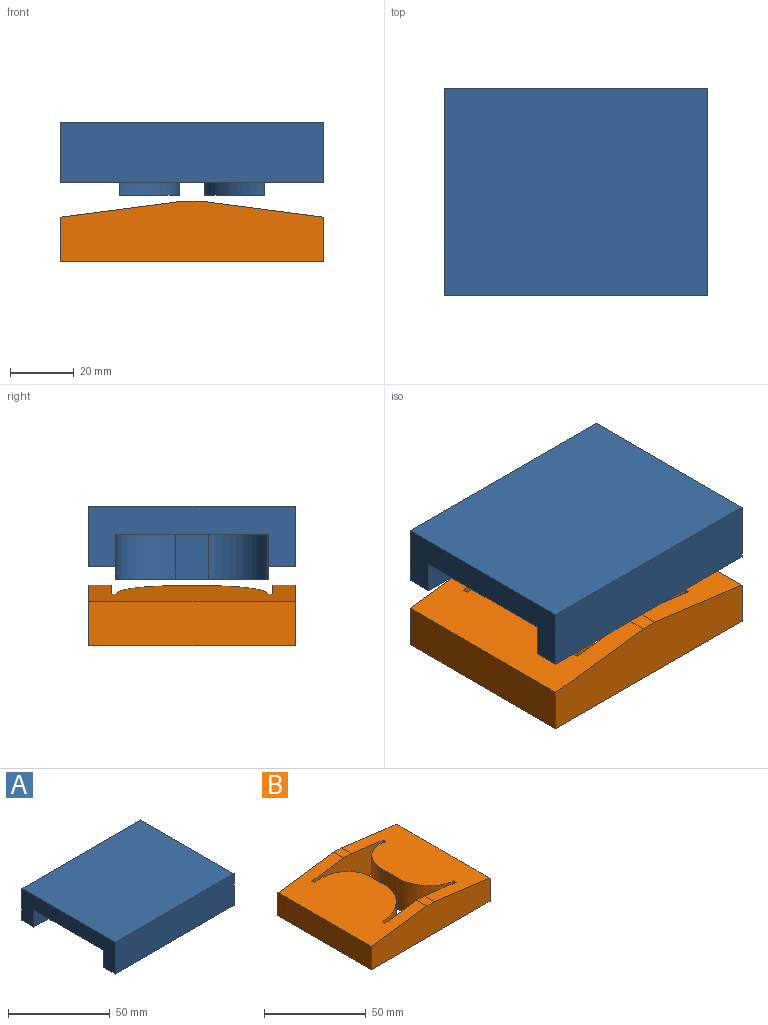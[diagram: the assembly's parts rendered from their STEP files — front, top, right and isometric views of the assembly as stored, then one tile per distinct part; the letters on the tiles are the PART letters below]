
ASSEMBLY  parts=2 mates=1
PART A: 30 faces, bbox 82.6x64.8x22.9 mm
  f0: plane 18.42x10.16mm, normal (0,-1,0), area 187.1mm2, adj f2,f8,f16,f28
  f1: plane 18.42x10.16mm, normal (0,1,0), area 187.1mm2, adj f2,f8,f15,f28
  f2: plane 64.77x19.05mm, normal (-1,0,0), area 743.5mm2, adj f0,f1,f3,f7,f8,f28,f29
  f3: plane 82.55x19.05mm, normal (0,-1,0), area 1572.6mm2, adj f2,f4,f8,f29
  f4: plane 64.77x19.05mm, normal (1,0,0), area 743.5mm2, adj f3,f5,f6,f7,f8,f27,f29
  f5: plane 18.42x10.16mm, normal (0,1,0), area 187.1mm2, adj f4,f8,f24,f27
  f6: plane 18.42x10.16mm, normal (0,-1,0), area 187.1mm2, adj f4,f8,f23,f27
  f7: plane 82.55x19.05mm, normal (0,1,0), area 1572.6mm2, adj f2,f4,f8,f29
  f8: plane 82.55x64.77mm, normal (0,0,-1), area 2042.2mm2, adj f0,f1,f2,f3,f4,f5,f6,f7
  f9: cylinder r=19.05mm len=19.05mm, axis (0,0,-1), area 114mm2, adj f8,f10,f15,f17
  f10: plane 10.16x3.81mm, normal (1,0,0), area 38.7mm2, adj f8,f9,f11,f17
  f11: cylinder r=19.05mm len=19.05mm, axis (0,0,-1), area 114mm2, adj f8,f10,f16,f17
  f12: cylinder r=18.54mm len=18.54mm, axis (0,0,-1), area 406.9mm2, adj f13,f16,f17,f28
  f13: plane 13.97x10.16mm, normal (-1,0,0), area 141.9mm2, adj f12,f14,f17,f28
  f14: cylinder r=18.54mm len=18.54mm, axis (0,0,-1), area 406.9mm2, adj f13,f15,f17,f28
  f15: plane 13.97x0.51mm, normal (-1,0,0), area 7.1mm2, adj f1,f9,f14,f17,f28
  f16: plane 13.97x0.51mm, normal (-1,0,0), area 7.1mm2, adj f0,f11,f12,f17,f28
  f17: plane 48.26x19.05mm, normal (0,0,-1), area 35.2mm2, adj f9,f10,f11,f12,f13,f14,f15,f16
  f18: cylinder r=19.05mm len=19.05mm, axis (0,0,-1), area 114mm2, adj f8,f19,f23,f26
  f19: plane 10.16x3.81mm, normal (-1,0,0), area 38.7mm2, adj f8,f18,f20,f26
  f20: cylinder r=19.05mm len=19.05mm, axis (0,0,-1), area 114mm2, adj f8,f19,f24,f26
  f21: plane 13.97x10.16mm, normal (1,0,0), area 141.9mm2, adj f22,f25,f26,f27
  f22: cylinder r=18.54mm len=18.54mm, axis (0,0,-1), area 406.9mm2, adj f21,f23,f26,f27
  f23: plane 13.97x0.51mm, normal (1,0,0), area 7.1mm2, adj f6,f18,f22,f26,f27
  f24: plane 13.97x0.51mm, normal (1,0,0), area 7.1mm2, adj f5,f20,f25,f26,f27
  f25: cylinder r=18.54mm len=18.54mm, axis (0,0,-1), area 406.9mm2, adj f21,f24,f26,f27
  f26: plane 48.26x19.05mm, normal (0,0,-1), area 35.2mm2, adj f18,f19,f20,f21,f22,f23,f24,f25
  f27: plane 48.26x36.96mm, normal (0,0,-1), area 1617.1mm2, adj f4,f5,f6,f21,f22,f23,f24,f25
  f28: plane 48.26x36.96mm, normal (0,0,-1), area 1617.1mm2, adj f0,f1,f2,f12,f13,f14,f15,f16
  f29: plane 82.55x64.77mm, normal (0,0,1), area 5346.8mm2, adj f2,f3,f4,f7
PART B: 25 faces, bbox 82.6x64.8x19.1 mm
  f0: plane 6.99x5.08mm, normal (0,0,1), area 35.5mm2, adj f1,f11,f23,f24
  f1: plane 82.55x19.05mm, normal (0,-1,0), area 1375.8mm2, adj f0,f2,f20,f22,f23,f24
  f2: plane 64.77x13.97mm, normal (1,0,0), area 904.8mm2, adj f1,f3,f22,f23
  f3: plane 82.55x19.05mm, normal (0,1,0), area 1375.8mm2, adj f2,f20,f21,f22,f23,f24
  f4: plane 16.14x1.78mm, normal (-1,0,0), area 28.7mm2, adj f5,f19,f22,f23
  f5: plane 16.39x1.87mm, normal (0,1,0), area 30.5mm2, adj f4,f6,f22,f23
  f6: cylinder r=18.54mm len=18.82mm, axis (0,0,-1), area 522.3mm2, adj f5,f7,f22,f23
  f7: plane 18.82x10.16mm, normal (-1,0,0), area 191.2mm2, adj f6,f8,f22,f23
  f8: cylinder r=18.54mm len=18.82mm, axis (0,0,-1), area 522.3mm2, adj f7,f9,f22,f23
  f9: plane 16.39x1.87mm, normal (0,-1,0), area 30.5mm2, adj f8,f10,f22,f23
  f10: plane 16.14x1.78mm, normal (-1,0,0), area 28.7mm2, adj f9,f11,f22,f23
  f11: plane 49.47x19.05mm, normal (0,1,0), area 877.8mm2, adj f0,f10,f12,f22,f23,f24
  f12: plane 16.14x1.78mm, normal (1,0,0), area 28.7mm2, adj f11,f13,f22,f24
  f13: plane 16.39x1.87mm, normal (0,-1,0), area 30.5mm2, adj f12,f14,f22,f24
  f14: cylinder r=18.54mm len=18.82mm, axis (0,0,-1), area 522.3mm2, adj f13,f15,f22,f24
  f15: plane 18.82x10.16mm, normal (1,0,0), area 191.2mm2, adj f14,f16,f22,f24
  f16: cylinder r=18.54mm len=18.82mm, axis (0,0,-1), area 522.3mm2, adj f15,f17,f22,f24
  f17: plane 16.39x1.87mm, normal (0,1,0), area 30.5mm2, adj f16,f18,f22,f24
  f18: plane 16.14x1.78mm, normal (1,0,0), area 28.7mm2, adj f17,f19,f22,f24
  f19: plane 49.47x19.05mm, normal (0,-1,0), area 877.8mm2, adj f4,f18,f21,f22,f23,f24
  f20: plane 64.77x13.97mm, normal (-1,0,0), area 904.8mm2, adj f1,f3,f22,f24
  f21: plane 6.99x5.08mm, normal (0,0,1), area 35.5mm2, adj f3,f19,f23,f24
  f22: plane 82.55x64.77mm, normal (0,0,-1), area 4467.7mm2, adj f1,f2,f3,f4,f5,f6,f7,f8
  f23: plane 64.77x38.74mm, normal (0.13,0,0.99), area 2217.2mm2, adj f0,f1,f2,f3,f4,f5,f6,f7
  f24: plane 64.77x38.74mm, normal (-0.13,0,0.99), area 2217.2mm2, adj f0,f1,f3,f11,f12,f13,f14,f15
PLACE A t=(0.12,0.91,-0.51)mm
PLACE B t=(0.12,0.91,-25.25)mm
MATE slider A.f26 <-> B.f22  axis (0,0,-1) through (4.44,-4.17,-4.32)mm
